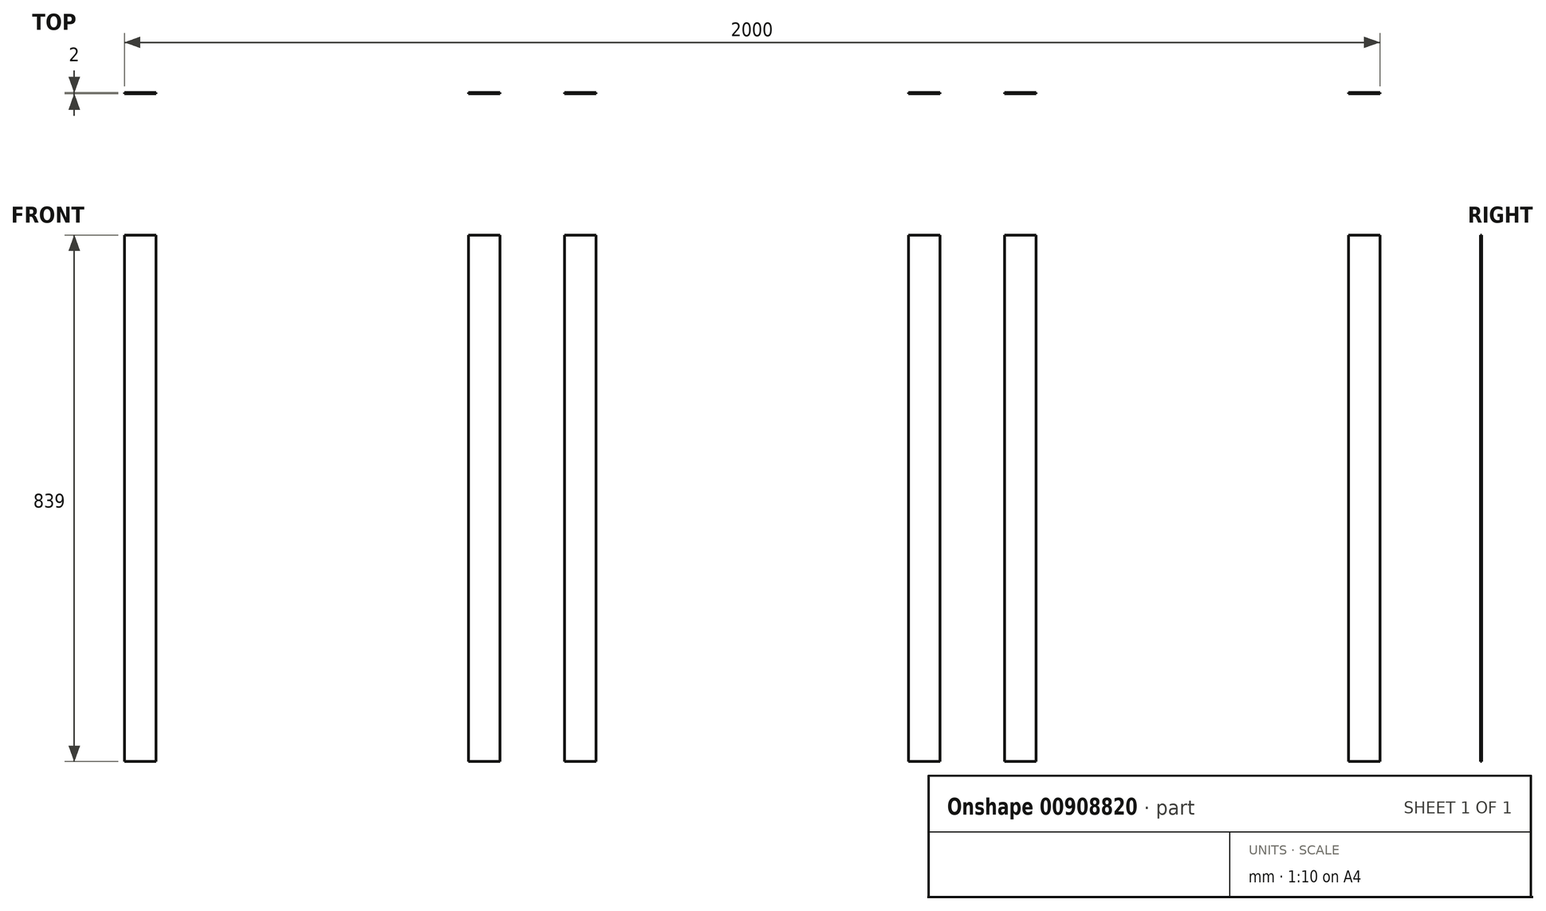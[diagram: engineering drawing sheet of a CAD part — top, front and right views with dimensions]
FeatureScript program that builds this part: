
annotation { "Feature Type Name" : "Feature", "Feature Type Description" : "" }
export const myFeature = defineFeature(function(context is Context, id is Id, definition is map)
    precondition{}
    {
        {
            var Q0;
            Q0=qCreatedBy(makeId("Front.planeOp"),FACE);
            var sketch = newSketch(context, id + "F0", { "sketchPlane" : qUnion([Q0])});
            skLineSegment(sketch, "E0.bottom", {"start": v(-548, 419.2) * mm, "end": v(-498, 419.2) * mm});
            skLineSegment(sketch, "E0.top", {"start": v(-548, -419.8) * mm, "end": v(-498, -419.8) * mm});
            skLineSegment(sketch, "E0.left", {"start": v(-548, 419.2) * mm, "end": v(-548, -419.8) * mm});
            skLineSegment(sketch, "E0.right", {"start": v(-498, 419.2) * mm, "end": v(-498, -419.8) * mm});
            skLineSegment(sketch, "E1.bottom", {"start": v(50, 419.2) * mm, "end": v(0, 419.2) * mm});
            skLineSegment(sketch, "E1.top", {"start": v(50, -419.8) * mm, "end": v(0, -419.8) * mm});
            skLineSegment(sketch, "E1.left", {"start": v(50, 419.2) * mm, "end": v(50, -419.8) * mm});
            skLineSegment(sketch, "E1.right", {"start": v(0, 419.2) * mm, "end": v(0, -419.8) * mm});
            skLineSegment(sketch, "E2.bottom", {"start": v(203, 419.2) * mm, "end": v(153, 419.2) * mm});
            skLineSegment(sketch, "E2.top", {"start": v(203, -419.8) * mm, "end": v(153, -419.8) * mm});
            skLineSegment(sketch, "E2.left", {"start": v(203, 419.2) * mm, "end": v(203, -419.8) * mm});
            skLineSegment(sketch, "E2.right", {"start": v(153, 419.2) * mm, "end": v(153, -419.8) * mm});
            skLineSegment(sketch, "E3.bottom", {"start": v(751, 419.2) * mm, "end": v(701, 419.2) * mm});
            skLineSegment(sketch, "E3.top", {"start": v(751, -419.8) * mm, "end": v(701, -419.8) * mm});
            skLineSegment(sketch, "E3.left", {"start": v(751, 419.2) * mm, "end": v(751, -419.8) * mm});
            skLineSegment(sketch, "E3.right", {"start": v(701, 419.2) * mm, "end": v(701, -419.8) * mm});
            skLineSegment(sketch, "E4.bottom", {"start": v(904, 419.2) * mm, "end": v(854, 419.2) * mm});
            skLineSegment(sketch, "E4.top", {"start": v(904, -419.8) * mm, "end": v(854, -419.8) * mm});
            skLineSegment(sketch, "E4.left", {"start": v(904, 419.2) * mm, "end": v(904, -419.8) * mm});
            skLineSegment(sketch, "E4.right", {"start": v(854, 419.2) * mm, "end": v(854, -419.8) * mm});
            skLineSegment(sketch, "E5.bottom", {"start": v(1452, 419.2) * mm, "end": v(1402, 419.2) * mm});
            skLineSegment(sketch, "E5.top", {"start": v(1452, -419.8) * mm, "end": v(1402, -419.8) * mm});
            skLineSegment(sketch, "E5.left", {"start": v(1452, 419.2) * mm, "end": v(1452, -419.8) * mm});
            skLineSegment(sketch, "E5.right", {"start": v(1402, 419.2) * mm, "end": v(1402, -419.8) * mm});
            skSolve(sketch);
        }
        {
            var Q0;
            Q0=makeQuery(id+"F0.imprint","IMPRINT",FACE,{"disambiguationData":[TD([[makeQuery(id+"F0.imprint","IMPRINT",EDGE,{"derivedFrom":sQuery(id+"F0.wireOp",EDGE,"E2.bottom")}),1.0]])]});
            var Q1;
            Q1=makeQuery(id+"F0.imprint","IMPRINT",FACE,{"disambiguationData":[TD([[makeQuery(id+"F0.imprint","IMPRINT",EDGE,{"derivedFrom":sQuery(id+"F0.wireOp",EDGE,"E4.bottom")}),1.0]])]});
            var Q2;
            Q2=makeQuery(id+"F0.imprint","IMPRINT",FACE,{"disambiguationData":[TD([[makeQuery(id+"F0.imprint","IMPRINT",EDGE,{"derivedFrom":sQuery(id+"F0.wireOp",EDGE,"E1.bottom")}),1.0]])]});
            var Q3;
            Q3=makeQuery(id+"F0.imprint","IMPRINT",FACE,{"disambiguationData":[TD([[makeQuery(id+"F0.imprint","IMPRINT",EDGE,{"derivedFrom":sQuery(id+"F0.wireOp",EDGE,"E3.bottom")}),1.0]])]});
            var Q4;
            Q4=makeQuery(id+"F0.imprint","IMPRINT",FACE,{"disambiguationData":[TD([[makeQuery(id+"F0.imprint","IMPRINT",EDGE,{"derivedFrom":sQuery(id+"F0.wireOp",EDGE,"E5.bottom")}),1.0]])]});
            var Q5;
            Q5=makeQuery(id+"F0.imprint","IMPRINT",FACE,{"disambiguationData":[TD([[makeQuery(id+"F0.imprint","IMPRINT",EDGE,{"derivedFrom":sQuery(id+"F0.wireOp",EDGE,"E0.bottom")}),-1.0]])]});
            extrude(context, id + "F1", {"entities" : qUnion([Q0, Q1, Q2, Q3, Q4, Q5]), "depth" : 2 * mm, "offsetDistance" : 25 * mm});
        }
    });
